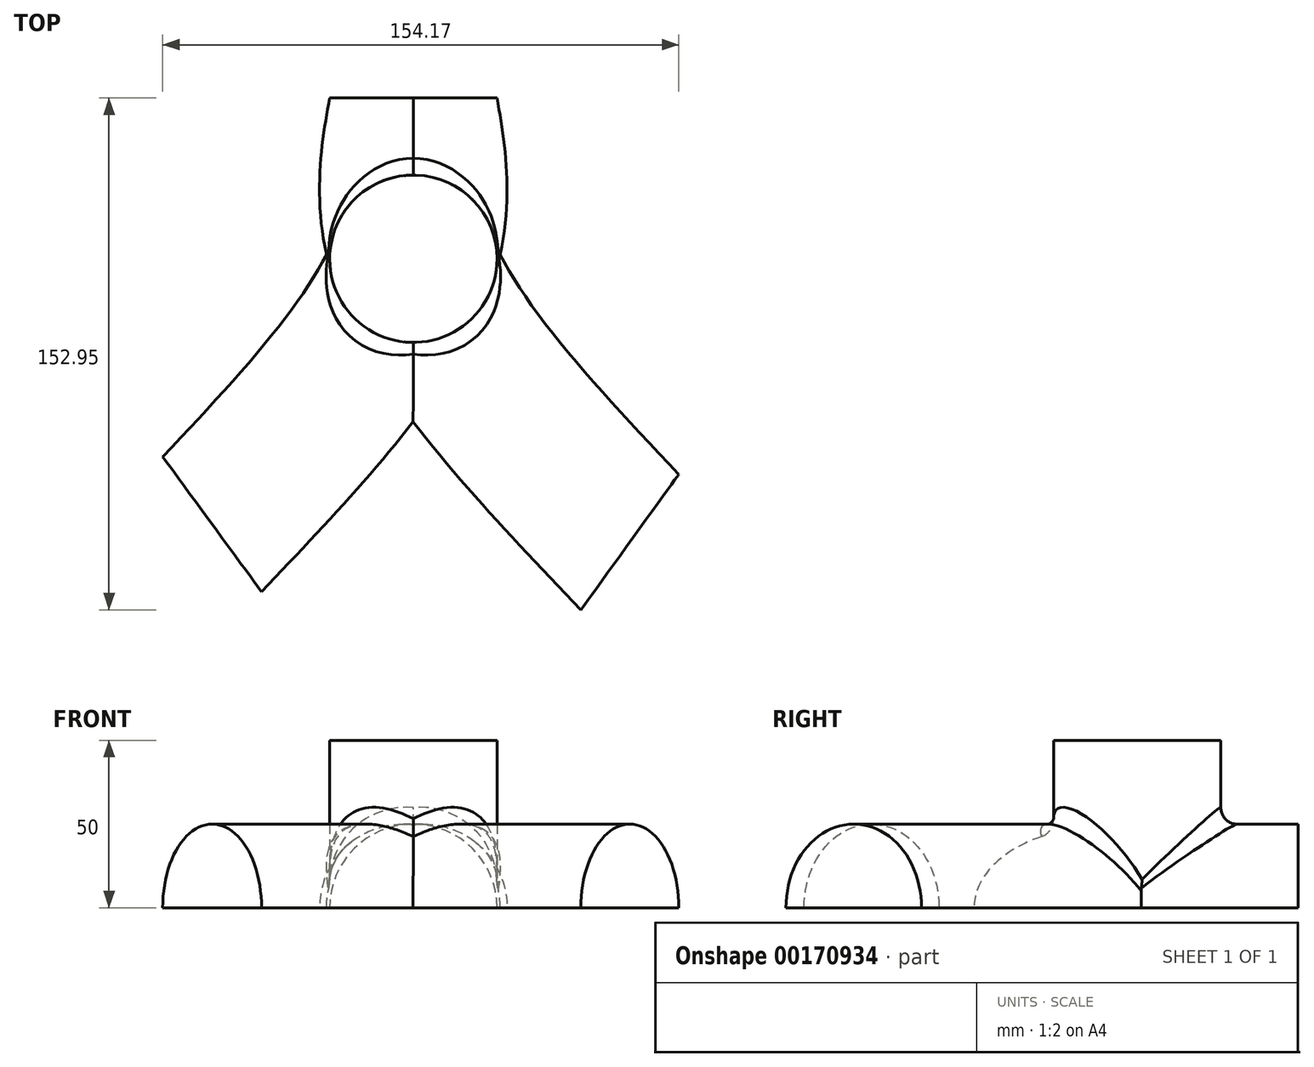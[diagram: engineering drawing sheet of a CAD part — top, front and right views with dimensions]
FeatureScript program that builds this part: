
annotation { "Feature Type Name" : "Feature", "Feature Type Description" : "" }
export const myFeature = defineFeature(function(context is Context, id is Id, definition is map)
    precondition{}
    {
        {
            var Q0;
            Q0=qCreatedBy(makeId("Front.planeOp"),FACE);
            var sketch = newSketch(context, id + "F0", { "sketchPlane" : qUnion([Q0])});
            skArc(sketch, "E0", {"start": v(25, 0) * mm, "mid": v(0, 25) * mm, "end": v(-25, 0) * mm});
            skLineSegment(sketch, "E1", {"start": v(-25, 0) * mm, "end": v(25, 0) * mm});
            skSolve(sketch);
        }
        {
            var Q0;
            Q0=qCreatedBy(makeId("Top.planeOp"),FACE);
            var sketch = newSketch(context, id + "F1", { "sketchPlane" : qUnion([Q0])});
            skCircle(sketch, "E2", {"center": v(0, -48.02) * mm, "radius": 25 * mm});
            skFitSpline(sketch, "E3", {"points": [v(0, 0) * mm, v(0, -48.02) * mm, v(-60.1, -127.36) * mm], "startDerivative": vector(20.87, -113.62) * mm, "endDerivative": vector(-131.9, -139.55) * mm});
            skFitSpline(sketch, "E4", {"points": [v(0, 0) * mm, v(0, -48.02) * mm, v(64.66, -132.69) * mm], "startDerivative": vector(-21.7, -115.14) * mm, "endDerivative": vector(140.4, -148.08) * mm});
            skSolve(sketch);
        }
        {
            var Q0;
            {var subQ0=sQuery(id+"F1.wireOp",EDGE,"E4");var subQ1=sQuery(id+"F1.wireOp",EDGE,"E2");var subQ2=makeQuery(id+"F1.imprint","INTERSECT",VERTEX,{"disambiguationData":[OD(0.0)],"derivedFrom":[subQ1,subQ0]});Q0=makeQuery(id+"F1.imprint","IMPRINT",FACE,{"disambiguationData":[TD([[makeQuery(id+"F1.imprint","IMPRINT",EDGE,{"disambiguationData":[TD([[subQ2,-1.0]])],"derivedFrom":subQ1}),1.0]])]});}
            var Q1;
            {var subQ0=sQuery(id+"F1.wireOp",EDGE,"E3");var subQ1=sQuery(id+"F1.wireOp",EDGE,"E2");var subQ2=makeQuery(id+"F1.imprint","INTERSECT",VERTEX,{"disambiguationData":[OD(0.0)],"derivedFrom":[subQ1,subQ0]});Q1=makeQuery(id+"F1.imprint","IMPRINT",FACE,{"disambiguationData":[TD([[makeQuery(id+"F1.imprint","IMPRINT",EDGE,{"disambiguationData":[TD([[subQ2,-1.0]])],"derivedFrom":subQ1}),1.0]])]});}
            var Q2;
            {var subQ0=sQuery(id+"F1.wireOp",EDGE,"E3");var subQ1=sQuery(id+"F1.wireOp",EDGE,"E2");var subQ2=makeQuery(id+"F1.imprint","INTERSECT",VERTEX,{"disambiguationData":[OD(0.0)],"derivedFrom":[subQ1,subQ0]});Q2=makeQuery(id+"F1.imprint","IMPRINT",FACE,{"disambiguationData":[TD([[makeQuery(id+"F1.imprint","IMPRINT",EDGE,{"disambiguationData":[TD([[subQ2,1.0]])],"derivedFrom":subQ1}),1.0]])]});}
            var Q3;
            {var subQ0=sQuery(id+"F1.wireOp",EDGE,"E4");var subQ1=sQuery(id+"F1.wireOp",EDGE,"E2");var subQ2=makeQuery(id+"F1.imprint","INTERSECT",VERTEX,{"disambiguationData":[OD(1.0)],"derivedFrom":[subQ1,subQ0]});Q3=makeQuery(id+"F1.imprint","IMPRINT",FACE,{"disambiguationData":[TD([[makeQuery(id+"F1.imprint","IMPRINT",EDGE,{"disambiguationData":[TD([[subQ2,1.0]])],"derivedFrom":subQ1}),1.0]])]});}
            extrude(context, id + "F2", {"entities" : qUnion([Q0, Q1, Q2, Q3]), "depth" : 50 * mm});
        }
        {
            var Q0;
            Q0=makeQuery(id+"F0.imprint","IMPRINT",FACE,{"disambiguationData":[TD([[makeQuery(id+"F0.imprint","IMPRINT",EDGE,{"derivedFrom":sQuery(id+"F0.wireOp",EDGE,"E0")}),1.0]])]});
            var Q1;
            Q1=sQuery(id+"F1.wireOp",EDGE,"E3");
            sweep(context, id + "F3", {"profiles" : qUnion([Q0]), "path" : qUnion([Q1])});
        }
        {
            var Q0;
            Q0=makeQuery(id+"F3.opSweep","CAP_FACE",FACE,{"disambiguationData":[OSD([sQuery(id+"F0.wireOp",EDGE,"E0"),sQuery(id+"F0.wireOp",EDGE,"E1"),sQuery(id+"F1.wireOp",VERTEX,"E3.start")])],"isStart":true});
            var Q1;
            Q1=sQuery(id+"F1.wireOp",EDGE,"E4");
            sweep(context, id + "F4", {"profiles" : qUnion([Q0]), "path" : qUnion([Q1])});
        }
        {
            var Q0;
            Q0=makeQuery(id+"F3.opSweep","SWEPT_BODY",BODY,{"disambiguationData":[OSD([sQuery(id+"F0.wireOp",EDGE,"E0"),sQuery(id+"F0.wireOp",EDGE,"E1"),sQuery(id+"F1.wireOp",EDGE,"E3")])]});
            var Q1;
            Q1=makeQuery(id+"F4.opSweep","SWEPT_BODY",BODY,{"disambiguationData":[OSD([sQuery(id+"F0.wireOp",EDGE,"E0"),sQuery(id+"F0.wireOp",EDGE,"E1"),sQuery(id+"F1.wireOp",VERTEX,"E3.start"),sQuery(id+"F1.wireOp",EDGE,"E4")])]});
            booleanBodies(context, id + "F5", {"operationType" : BooleanOperationType.UNION, "tools" : qUnion([Q0, Q1])});
        }
        {
            var Q0;
            Q0=makeQuery(id+"F2.opExtrude","SWEPT_BODY",BODY,{"disambiguationData":[OSD([sQuery(id+"F1.wireOp",EDGE,"E2")])]});
            var Q1;
            Q1=makeQuery(id+"F3.opSweep","SWEPT_BODY",BODY,{"disambiguationData":[OSD([sQuery(id+"F0.wireOp",EDGE,"E0"),sQuery(id+"F0.wireOp",EDGE,"E1"),sQuery(id+"F1.wireOp",EDGE,"E3")])]});
            booleanBodies(context, id + "F6", {"operationType" : BooleanOperationType.UNION, "tools" : qUnion([Q0, Q1])});
        }
        {
            var Q0;
            {var subQ2=sQuery(id+"F0.wireOp",EDGE,"E0");var subQ3=sQuery(id+"F1.wireOp",EDGE,"E3");var subQ4=sQuery(id+"F0.wireOp",EDGE,"E1");var subQ5=makeQuery(id+"F3.opSweep","SWEPT_FACE",FACE,{"disambiguationData":[OSD([subQ2,subQ3])]});Q0=makeQuery(id+"F6.opBoolean","INTERSECT",EDGE,{"derivedFrom":[makeQuery(id+"F2.opExtrude","SWEPT_FACE",FACE,{"disambiguationData":[OSD([sQuery(id+"F1.wireOp",EDGE,"E2")])]}),makeQuery(id+"F5.opBoolean","SPLIT",FACE,{"disambiguationData":[TD([makeQuery(id+"F3.opSweep","CAP_FACE",FACE,{"disambiguationData":[OSD([subQ2,subQ4,sQuery(id+"F1.wireOp",VERTEX,"E3.end")])],"isStart":false})])],"derivedFrom":subQ5})]});}
            var Q1;
            {var subQ0=sQuery(id+"F1.wireOp",EDGE,"E4");var subQ1=sQuery(id+"F1.wireOp",VERTEX,"E3.start");var subQ2=sQuery(id+"F0.wireOp",EDGE,"E0");var subQ3=makeQuery(id+"F4.opSweep","SWEPT_FACE",FACE,{"disambiguationData":[OSD([subQ2,subQ1,subQ0])]});var subQ4=sQuery(id+"F0.wireOp",EDGE,"E1");Q1=makeQuery(id+"F6.opBoolean","INTERSECT",EDGE,{"derivedFrom":[makeQuery(id+"F2.opExtrude","SWEPT_FACE",FACE,{"disambiguationData":[OSD([sQuery(id+"F1.wireOp",EDGE,"E2")])]}),makeQuery(id+"F5.opBoolean","SPLIT",FACE,{"disambiguationData":[TD([makeQuery(id+"F4.opSweep","CAP_FACE",FACE,{"disambiguationData":[OSD([subQ2,subQ4,subQ1,sQuery(id+"F1.wireOp",VERTEX,"E4.end")])],"isStart":false})])],"derivedFrom":subQ3})]});}
            var Q2;
            {var subQ1=sQuery(id+"F1.wireOp",VERTEX,"E3.start");var subQ2=sQuery(id+"F0.wireOp",EDGE,"E0");var subQ3=sQuery(id+"F1.wireOp",EDGE,"E3");var subQ4=sQuery(id+"F0.wireOp",EDGE,"E1");var subQ5=makeQuery(id+"F3.opSweep","SWEPT_FACE",FACE,{"disambiguationData":[OSD([subQ2,subQ3])]});Q2=makeQuery(id+"F6.opBoolean","INTERSECT",EDGE,{"derivedFrom":[makeQuery(id+"F2.opExtrude","SWEPT_FACE",FACE,{"disambiguationData":[OSD([sQuery(id+"F1.wireOp",EDGE,"E2")])]}),makeQuery(id+"F5.opBoolean","SPLIT",FACE,{"disambiguationData":[TD([makeQuery(id+"F3.opSweep","CAP_FACE",FACE,{"disambiguationData":[OSD([subQ2,subQ4,subQ1])],"isStart":true})])],"derivedFrom":subQ5})]});}
            var Q3;
            {var subQ0=sQuery(id+"F1.wireOp",EDGE,"E4");var subQ1=sQuery(id+"F1.wireOp",VERTEX,"E3.start");var subQ2=sQuery(id+"F0.wireOp",EDGE,"E0");var subQ3=makeQuery(id+"F4.opSweep","SWEPT_FACE",FACE,{"disambiguationData":[OSD([subQ2,subQ1,subQ0])]});var subQ5=sQuery(id+"F0.wireOp",EDGE,"E1");Q3=makeQuery(id+"F6.opBoolean","INTERSECT",EDGE,{"derivedFrom":[makeQuery(id+"F2.opExtrude","SWEPT_FACE",FACE,{"disambiguationData":[OSD([sQuery(id+"F1.wireOp",EDGE,"E2")])]}),makeQuery(id+"F5.opBoolean","SPLIT",FACE,{"disambiguationData":[TD([makeQuery(id+"F3.opSweep","CAP_FACE",FACE,{"disambiguationData":[OSD([subQ2,subQ5,subQ1])],"isStart":true})])],"derivedFrom":subQ3})]});}
            fillet(context, id + "F7", {"entities" : qUnion([Q0, Q1, Q2, Q3]), "radius" : 5 * mm, "tangentPropagation" : true, "allowEdgeOverflow" : false});
        }
    });
